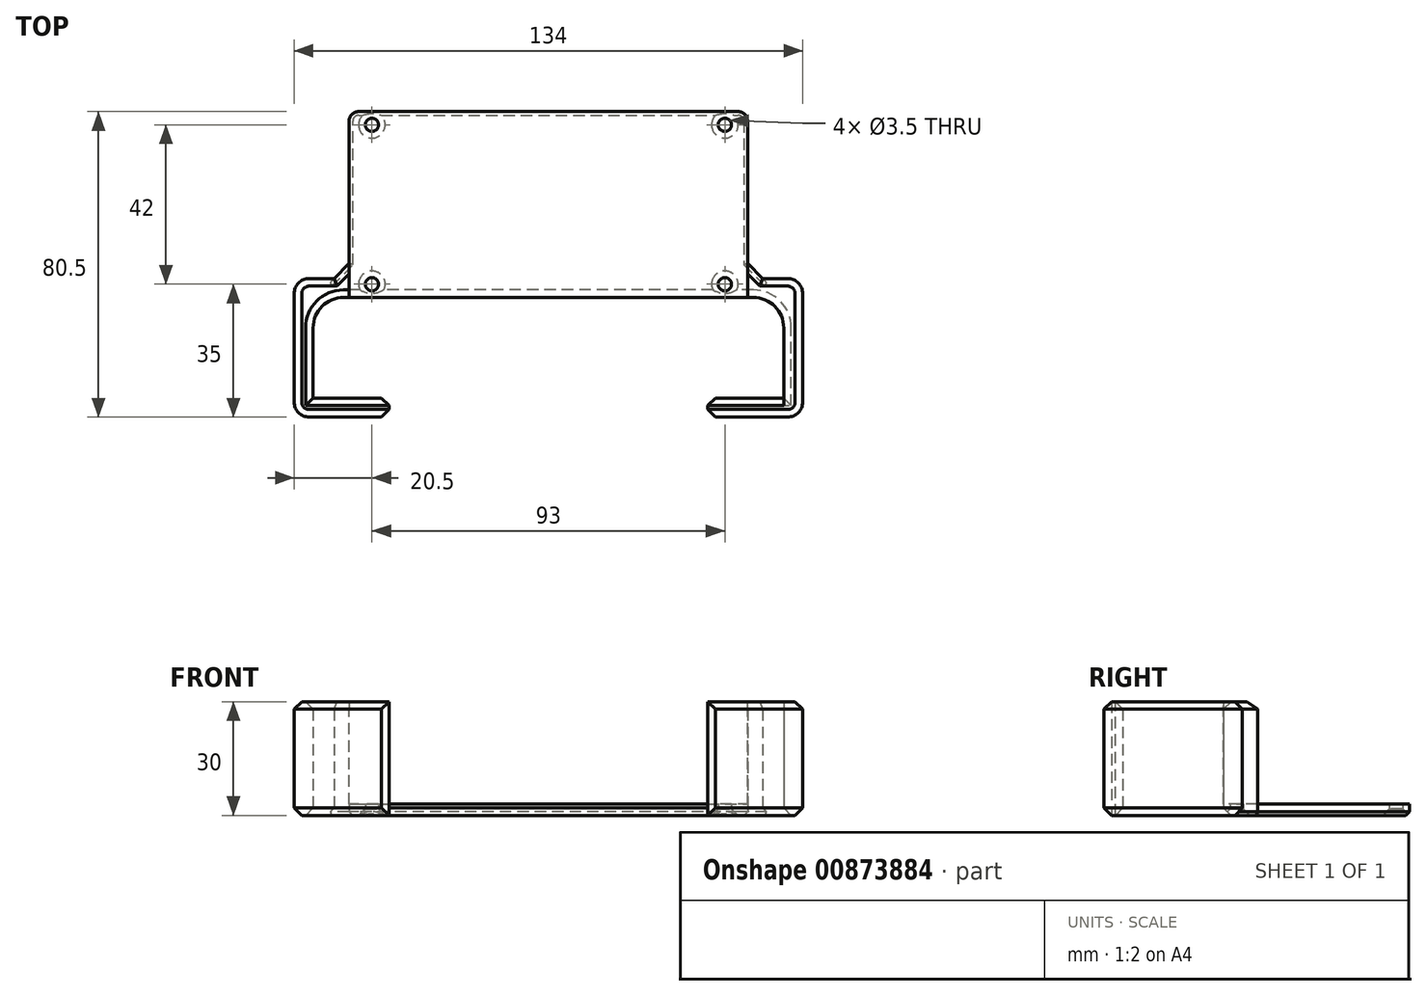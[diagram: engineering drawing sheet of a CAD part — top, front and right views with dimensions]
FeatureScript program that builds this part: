
annotation { "Feature Type Name" : "Feature", "Feature Type Description" : "" }
export const myFeature = defineFeature(function(context is Context, id is Id, definition is map)
    precondition{}
    {
        {
            var Q0;
            Q0=qCreatedBy(makeId("Top.planeOp"),FACE);
            var sketch = newSketch(context, id + "F0", { "sketchPlane" : qUnion([Q0])});
            skLineSegment(sketch, "E0.bottom", {"start": v(0, 0) * mm, "end": v(105, 0) * mm});
            skLineSegment(sketch, "E0.top", {"start": v(2.5, 49) * mm, "end": v(102.5, 49) * mm});
            skLineSegment(sketch, "E0.left", {"start": v(0, 9) * mm, "end": v(0, 46.5) * mm});
            skLineSegment(sketch, "E0.right", {"start": v(105, 9) * mm, "end": v(105, 46.5) * mm});
            skLineSegment(sketch, "E1.bottom", {"start": v(-1.5, 0) * mm, "end": v(106.5, 0) * mm});
            skLineSegment(sketch, "E1.top", {"start": v(-9.5, -26.5) * mm, "end": v(10.5, -26.5) * mm});
            skLineSegment(sketch, "E1.left", {"start": v(-9.5, -8) * mm, "end": v(-9.5, -26.5) * mm});
            skLineSegment(sketch, "E1.right", {"start": v(114.5, -8) * mm, "end": v(114.5, -26.5) * mm});
            skLineSegment(sketch, "E2.0", {"start": v(-10.5, 5) * mm, "end": v(-4, 5) * mm});
            skLineSegment(sketch, "E2.1", {"start": v(-14.5, 1) * mm, "end": v(-14.5, -27.5) * mm});
            skLineSegment(sketch, "E2.2", {"start": v(-10.5, -31.5) * mm, "end": v(10.5, -31.5) * mm});
            skLineSegment(sketch, "E2.3", {"start": v(119.5, 1) * mm, "end": v(119.5, -27.5) * mm});
            skLineSegment(sketch, "E3", {"start": v(10.5, -26.5) * mm, "end": v(10.5, -38.4) * mm});
            skLineSegment(sketch, "E4", {"start": v(94.5, -26.5) * mm, "end": v(94.5, -38.4) * mm});
            skLineSegment(sketch, "E5.trimOffspring", {"start": v(94.5, -26.5) * mm, "end": v(114.5, -26.5) * mm});
            skLineSegment(sketch, "E6.trimOffspring", {"start": v(94.5, -31.5) * mm, "end": v(115.5, -31.5) * mm});
            skLineSegment(sketch, "E7.trimOffspring", {"start": v(109, 5) * mm, "end": v(115.5, 5) * mm});
            skLineSegment(sketch, "E8", {"start": v(-4, 5) * mm, "end": v(0, 9) * mm});
            skPoint(sketch, "E9.orphan", {"position": v(0, 5) * mm});
            skLineSegment(sketch, "E10", {"start": v(105, 9) * mm, "end": v(109, 5) * mm});
            skPoint(sketch, "E11.visualSharp", {"position": v(-14.5, 5) * mm});
            skArc(sketch, "E11.filletArc", {"start": v(-10.5, 5) * mm, "mid": v(-13.33, 3.83) * mm, "end": v(-14.5, 1) * mm});
            skPoint(sketch, "E12.visualSharp", {"position": v(-14.5, -31.5) * mm});
            skArc(sketch, "E12.filletArc", {"start": v(-14.5, -27.5) * mm, "mid": v(-13.33, -30.33) * mm, "end": v(-10.5, -31.5) * mm});
            skPoint(sketch, "E13.visualSharp", {"position": v(119.5, -31.5) * mm});
            skArc(sketch, "E13.filletArc", {"start": v(115.5, -31.5) * mm, "mid": v(118.33, -30.33) * mm, "end": v(119.5, -27.5) * mm});
            skPoint(sketch, "E14.visualSharp", {"position": v(119.5, 5) * mm});
            skArc(sketch, "E14.filletArc", {"start": v(119.5, 1) * mm, "mid": v(118.33, 3.83) * mm, "end": v(115.5, 5) * mm});
            skPoint(sketch, "E15.visualSharp", {"position": v(0, 49) * mm});
            skArc(sketch, "E15.filletArc", {"start": v(2.5, 49) * mm, "mid": v(0.73, 48.27) * mm, "end": v(0, 46.5) * mm});
            skPoint(sketch, "E16.visualSharp", {"position": v(105, 49) * mm});
            skArc(sketch, "E16.filletArc", {"start": v(105, 46.5) * mm, "mid": v(104.27, 48.27) * mm, "end": v(102.5, 49) * mm});
            skPoint(sketch, "E17.visualSharp", {"position": v(-9.5, 0) * mm});
            skArc(sketch, "E17.filletArc", {"start": v(-1.5, 0) * mm, "mid": v(-7.16, -2.34) * mm, "end": v(-9.5, -8) * mm});
            skPoint(sketch, "E18.visualSharp", {"position": v(114.5, 0) * mm});
            skArc(sketch, "E18.filletArc", {"start": v(114.5, -8) * mm, "mid": v(112.16, -2.34) * mm, "end": v(106.5, 0) * mm});
            skSolve(sketch);
        }
        {
            var Q0;
            Q0=makeQuery(id+"F0.imprint","IMPRINT",FACE,{"disambiguationData":[TD([[makeQuery(id+"F0.imprint","IMPRINT",EDGE,{"derivedFrom":sQuery(id+"F0.wireOp",EDGE,"E0.top")}),-1.0]])]});
            extrude(context, id + "F1", {"entities" : qUnion([Q0]), "depth" : 30 * mm, "offsetDistance" : 25 * mm});
        }
        {
            var Q0;
            Q0=makeQuery(id+"F1.opExtrude","CAP_FACE",FACE,{"disambiguationData":[OSD([sQuery(id+"F0.wireOp",EDGE,"E0.top"),sQuery(id+"F0.wireOp",EDGE,"E0.left"),sQuery(id+"F0.wireOp",EDGE,"E0.right"),sQuery(id+"F0.wireOp",EDGE,"E1.bottom"),sQuery(id+"F0.wireOp",EDGE,"E1.top"),sQuery(id+"F0.wireOp",EDGE,"E1.left"),sQuery(id+"F0.wireOp",EDGE,"E1.right"),sQuery(id+"F0.wireOp",EDGE,"E2.0"),sQuery(id+"F0.wireOp",EDGE,"E2.1"),sQuery(id+"F0.wireOp",EDGE,"E2.2"),sQuery(id+"F0.wireOp",EDGE,"E2.3"),sQuery(id+"F0.wireOp",EDGE,"E3"),sQuery(id+"F0.wireOp",EDGE,"E4"),sQuery(id+"F0.wireOp",EDGE,"E5.trimOffspring"),sQuery(id+"F0.wireOp",EDGE,"E6.trimOffspring"),sQuery(id+"F0.wireOp",EDGE,"E7.trimOffspring"),sQuery(id+"F0.wireOp",EDGE,"E8"),sQuery(id+"F0.wireOp",EDGE,"E10"),sQuery(id+"F0.wireOp",EDGE,"E11.filletArc"),sQuery(id+"F0.wireOp",EDGE,"E12.filletArc"),sQuery(id+"F0.wireOp",EDGE,"E13.filletArc"),sQuery(id+"F0.wireOp",EDGE,"E14.filletArc"),sQuery(id+"F0.wireOp",EDGE,"E15.filletArc"),sQuery(id+"F0.wireOp",EDGE,"E16.filletArc"),sQuery(id+"F0.wireOp",EDGE,"E17.filletArc"),sQuery(id+"F0.wireOp",EDGE,"E18.filletArc")])],"isStart":false});
            var sketch = newSketch(context, id + "F2", { "sketchPlane" : qUnion([Q0])});
            skLineSegment(sketch, "E19.0.0", {"start": v(114.5, -26.5) * mm, "end": v(94.5, -26.5) * mm});
            skLineSegment(sketch, "E19.0.1", {"start": v(94.5, -26.5) * mm, "end": v(94.5, -31.5) * mm});
            skLineSegment(sketch, "E19.0.2", {"start": v(94.5, -31.5) * mm, "end": v(115.5, -31.5) * mm});
            skArc(sketch, "E19.0.3", {"start": v(115.5, -31.5) * mm, "mid": v(118.33, -30.33) * mm, "end": v(119.5, -27.5) * mm});
            skLineSegment(sketch, "E19.0.4", {"start": v(119.5, -27.5) * mm, "end": v(119.5, 1) * mm});
            skArc(sketch, "E19.0.5", {"start": v(119.5, 1) * mm, "mid": v(118.33, 3.83) * mm, "end": v(115.5, 5) * mm});
            skLineSegment(sketch, "E19.0.6", {"start": v(115.5, 5) * mm, "end": v(109, 5) * mm});
            skLineSegment(sketch, "E19.0.7", {"start": v(109, 5) * mm, "end": v(105, 9) * mm});
            skLineSegment(sketch, "E19.0.8", {"start": v(105, 9) * mm, "end": v(105, 46.5) * mm});
            skArc(sketch, "E19.0.9", {"start": v(105, 46.5) * mm, "mid": v(104.27, 48.27) * mm, "end": v(102.5, 49) * mm});
            skLineSegment(sketch, "E19.0.10", {"start": v(102.5, 49) * mm, "end": v(2.5, 49) * mm});
            skArc(sketch, "E19.0.11", {"start": v(2.5, 49) * mm, "mid": v(0.73, 48.27) * mm, "end": v(0, 46.5) * mm});
            skLineSegment(sketch, "E19.0.12", {"start": v(0, 46.5) * mm, "end": v(0, 9) * mm});
            skLineSegment(sketch, "E19.0.13", {"start": v(0, 9) * mm, "end": v(-4, 5) * mm});
            skLineSegment(sketch, "E19.0.14", {"start": v(-4, 5) * mm, "end": v(-10.5, 5) * mm});
            skArc(sketch, "E19.0.15", {"start": v(-10.5, 5) * mm, "mid": v(-13.33, 3.83) * mm, "end": v(-14.5, 1) * mm});
            skLineSegment(sketch, "E19.0.16", {"start": v(-14.5, 1) * mm, "end": v(-14.5, -27.5) * mm});
            skArc(sketch, "E19.0.17", {"start": v(-14.5, -27.5) * mm, "mid": v(-13.33, -30.33) * mm, "end": v(-10.5, -31.5) * mm});
            skLineSegment(sketch, "E19.0.18", {"start": v(-10.5, -31.5) * mm, "end": v(10.5, -31.5) * mm});
            skLineSegment(sketch, "E19.0.19", {"start": v(10.5, -31.5) * mm, "end": v(10.5, -26.5) * mm});
            skLineSegment(sketch, "E19.0.20", {"start": v(10.5, -26.5) * mm, "end": v(-9.5, -26.5) * mm});
            skLineSegment(sketch, "E19.0.21", {"start": v(-9.5, -26.5) * mm, "end": v(-9.5, -8) * mm});
            skArc(sketch, "E19.0.22", {"start": v(-9.5, -8) * mm, "mid": v(-7.16, -2.34) * mm, "end": v(-1.5, 0) * mm});
            skLineSegment(sketch, "E19.0.23", {"start": v(-1.5, 0) * mm, "end": v(106.5, 0) * mm});
            skArc(sketch, "E19.0.24", {"start": v(106.5, 0) * mm, "mid": v(112.16, -2.34) * mm, "end": v(114.5, -8) * mm});
            skLineSegment(sketch, "E19.0.25", {"start": v(114.5, -8) * mm, "end": v(114.5, -26.5) * mm});
            skLineSegment(sketch, "E20.bottom", {"start": v(0, 49.1) * mm, "end": v(105, 49.1) * mm});
            skLineSegment(sketch, "E20.left", {"start": v(0, 49.1) * mm, "end": v(0, 5) * mm});
            skLineSegment(sketch, "E20.right", {"start": v(105, 49.1) * mm, "end": v(105, 5) * mm});
            skLineSegment(sketch, "E21.top", {"start": v(0, 0) * mm, "end": v(105, 0) * mm});
            skLineSegment(sketch, "E21.left", {"start": v(0, 5) * mm, "end": v(0, 0) * mm});
            skLineSegment(sketch, "E21.right", {"start": v(105, 5) * mm, "end": v(105, 0) * mm});
            skSolve(sketch);
        }
        {
            var Q0;
            {var subQ4=sQuery(id+"F2.wireOp",EDGE,"E19.0.9");Q0=makeQuery(id+"F2.imprint","IMPRINT",FACE,{"disambiguationData":[TD([[makeQuery(id+"F2.imprint","IMPRINT",EDGE,{"derivedFrom":subQ4}),1.0]])]});}
            extrude(context, id + "F3", {"entities" : qUnion([Q0]), "operationType" : NewBodyOperationType.REMOVE, "oppositeDirection" : true, "depth" : 27 * mm, "offsetDistance" : 25 * mm});
        }
        {
            var Q0;
            Q0=makeQuery(id+"F1.opExtrude","SWEPT_EDGE",EDGE,{"disambiguationData":[OSD([sQuery(id+"F0.wireOp",EDGE,"E4"),sQuery(id+"F0.wireOp",EDGE,"E5.trimOffspring")])]});
            var Q1;
            Q1=makeQuery(id+"F1.opExtrude","SWEPT_EDGE",EDGE,{"disambiguationData":[OSD([sQuery(id+"F0.wireOp",EDGE,"E4"),sQuery(id+"F0.wireOp",EDGE,"E6.trimOffspring")])]});
            var Q2;
            Q2=makeQuery(id+"F1.opExtrude","SWEPT_EDGE",EDGE,{"disambiguationData":[OSD([sQuery(id+"F0.wireOp",EDGE,"E2.2"),sQuery(id+"F0.wireOp",EDGE,"E3")])]});
            var Q3;
            Q3=makeQuery(id+"F1.opExtrude","SWEPT_EDGE",EDGE,{"disambiguationData":[OSD([sQuery(id+"F0.wireOp",EDGE,"E1.top"),sQuery(id+"F0.wireOp",EDGE,"E3")])]});
            chamfer(context, id + "F4", {"entities" : qUnion([Q0, Q1, Q2, Q3]), "width" : 2 * mm, "tangentPropagation" : true});
        }
        {
            var Q0;
            Q0=makeQuery(id+"F1.opExtrude","CAP_EDGE",EDGE,{"disambiguationData":[OSD([sQuery(id+"F0.wireOp",EDGE,"E5.trimOffspring")])],"isStart":true});
            var Q1;
            Q1=makeQuery(id+"F1.opExtrude","CAP_EDGE",EDGE,{"disambiguationData":[OSD([sQuery(id+"F0.wireOp",EDGE,"E1.top")])],"isStart":true});
            var Q2;
            Q2=makeQuery(id+"F1.opExtrude","CAP_EDGE",EDGE,{"disambiguationData":[OSD([sQuery(id+"F0.wireOp",EDGE,"E2.2")])],"isStart":true});
            var Q3;
            Q3=makeQuery(id+"F1.opExtrude","CAP_EDGE",EDGE,{"disambiguationData":[OSD([sQuery(id+"F0.wireOp",EDGE,"E6.trimOffspring")])],"isStart":true});
            var Q4;
            Q4=makeQuery(id+"F1.opExtrude","CAP_EDGE",EDGE,{"disambiguationData":[OSD([sQuery(id+"F0.wireOp",EDGE,"E2.0")])],"isStart":false});
            var Q5;
            Q5=makeQuery(id+"F1.opExtrude","CAP_EDGE",EDGE,{"disambiguationData":[OSD([sQuery(id+"F0.wireOp",EDGE,"E1.left")])],"isStart":false});
            var Q6;
            Q6=makeQuery(id+"F1.opExtrude","CAP_EDGE",EDGE,{"disambiguationData":[OSD([sQuery(id+"F0.wireOp",EDGE,"E1.top")])],"isStart":false});
            var Q7;
            Q7=makeQuery(id+"F1.opExtrude","CAP_EDGE",EDGE,{"disambiguationData":[OSD([sQuery(id+"F0.wireOp",EDGE,"E5.trimOffspring")])],"isStart":false});
            var Q8;
            Q8=makeQuery(id+"F1.opExtrude","CAP_EDGE",EDGE,{"disambiguationData":[OSD([sQuery(id+"F0.wireOp",EDGE,"E6.trimOffspring")])],"isStart":false});
            var Q9;
            Q9=makeQuery(id+"F1.opExtrude","CAP_EDGE",EDGE,{"disambiguationData":[OSD([sQuery(id+"F0.wireOp",EDGE,"E10")])],"isStart":false});
            var Q10;
            Q10=makeQuery(id+"F1.opExtrude","CAP_EDGE",EDGE,{"disambiguationData":[OSD([sQuery(id+"F0.wireOp",EDGE,"E8")])],"isStart":false});
            chamfer(context, id + "F5", {"entities" : qUnion([Q0, Q1, Q2, Q3, Q4, Q5, Q6, Q7, Q8, Q9, Q10]), "width" : 2 * mm, "tangentPropagation" : true});
        }
        {
            var Q0;
            Q0=makeQuery(id+"F1.opExtrude","CAP_FACE",FACE,{"disambiguationData":[OSD([sQuery(id+"F0.wireOp",EDGE,"E0.top"),sQuery(id+"F0.wireOp",EDGE,"E0.left"),sQuery(id+"F0.wireOp",EDGE,"E0.right"),sQuery(id+"F0.wireOp",EDGE,"E1.bottom"),sQuery(id+"F0.wireOp",EDGE,"E1.top"),sQuery(id+"F0.wireOp",EDGE,"E1.left"),sQuery(id+"F0.wireOp",EDGE,"E1.right"),sQuery(id+"F0.wireOp",EDGE,"E2.0"),sQuery(id+"F0.wireOp",EDGE,"E2.1"),sQuery(id+"F0.wireOp",EDGE,"E2.2"),sQuery(id+"F0.wireOp",EDGE,"E2.3"),sQuery(id+"F0.wireOp",EDGE,"E3"),sQuery(id+"F0.wireOp",EDGE,"E4"),sQuery(id+"F0.wireOp",EDGE,"E5.trimOffspring"),sQuery(id+"F0.wireOp",EDGE,"E6.trimOffspring"),sQuery(id+"F0.wireOp",EDGE,"E7.trimOffspring"),sQuery(id+"F0.wireOp",EDGE,"E8"),sQuery(id+"F0.wireOp",EDGE,"E10"),sQuery(id+"F0.wireOp",EDGE,"E11.filletArc"),sQuery(id+"F0.wireOp",EDGE,"E12.filletArc"),sQuery(id+"F0.wireOp",EDGE,"E13.filletArc"),sQuery(id+"F0.wireOp",EDGE,"E14.filletArc"),sQuery(id+"F0.wireOp",EDGE,"E15.filletArc"),sQuery(id+"F0.wireOp",EDGE,"E16.filletArc"),sQuery(id+"F0.wireOp",EDGE,"E17.filletArc"),sQuery(id+"F0.wireOp",EDGE,"E18.filletArc")])],"isStart":true});
            var sketch = newSketch(context, id + "F6", { "sketchPlane" : qUnion([Q0])});
            skLineSegment(sketch, "E22.0.0", {"start": v(105, -9) * mm, "end": v(111, -3) * mm});
            skLineSegment(sketch, "E22.0.1", {"start": v(111, -3) * mm, "end": v(115.5, -3) * mm});
            skArc(sketch, "E22.0.2", {"start": v(115.5, -3) * mm, "mid": v(116.91, -2.41) * mm, "end": v(117.5, -1) * mm});
            skLineSegment(sketch, "E22.0.3", {"start": v(117.5, -1) * mm, "end": v(117.5, 27.5) * mm});
            skArc(sketch, "E22.0.4", {"start": v(117.5, 27.5) * mm, "mid": v(116.91, 28.91) * mm, "end": v(115.5, 29.5) * mm});
            skLineSegment(sketch, "E22.0.5", {"start": v(115.5, 29.5) * mm, "end": v(94.5, 29.5) * mm});
            skLineSegment(sketch, "E22.0.6", {"start": v(94.5, 29.5) * mm, "end": v(94.5, 28.5) * mm});
            skLineSegment(sketch, "E22.0.7", {"start": v(94.5, 28.5) * mm, "end": v(116.5, 28.5) * mm});
            skLineSegment(sketch, "E22.0.8", {"start": v(116.5, 28.5) * mm, "end": v(116.5, 8) * mm});
            skArc(sketch, "E22.0.9", {"start": v(116.5, 8) * mm, "mid": v(113.57, 0.93) * mm, "end": v(106.5, -2) * mm});
            skLineSegment(sketch, "E22.0.10", {"start": v(106.5, -2) * mm, "end": v(-1.5, -2) * mm});
            skArc(sketch, "E22.0.11", {"start": v(-1.5, -2) * mm, "mid": v(-8.57, 0.93) * mm, "end": v(-11.5, 8) * mm});
            skLineSegment(sketch, "E22.0.12", {"start": v(-11.5, 8) * mm, "end": v(-11.5, 28.5) * mm});
            skLineSegment(sketch, "E22.0.13", {"start": v(-11.5, 28.5) * mm, "end": v(10.5, 28.5) * mm});
            skLineSegment(sketch, "E22.0.14", {"start": v(10.5, 28.5) * mm, "end": v(10.5, 29.5) * mm});
            skLineSegment(sketch, "E22.0.15", {"start": v(10.5, 29.5) * mm, "end": v(-10.5, 29.5) * mm});
            skArc(sketch, "E22.0.16", {"start": v(-10.5, 29.5) * mm, "mid": v(-11.91, 28.91) * mm, "end": v(-12.5, 27.5) * mm});
            skLineSegment(sketch, "E22.0.17", {"start": v(-12.5, 27.5) * mm, "end": v(-12.5, -1) * mm});
            skArc(sketch, "E22.0.18", {"start": v(-12.5, -1) * mm, "mid": v(-11.91, -2.41) * mm, "end": v(-10.5, -3) * mm});
            skLineSegment(sketch, "E22.0.19", {"start": v(-10.5, -3) * mm, "end": v(-6, -3) * mm});
            skLineSegment(sketch, "E22.0.20", {"start": v(-6, -3) * mm, "end": v(0, -9) * mm});
            skLineSegment(sketch, "E22.0.21", {"start": v(0, -9) * mm, "end": v(0, -46.5) * mm});
            skArc(sketch, "E22.0.22", {"start": v(0, -46.5) * mm, "mid": v(0.73, -48.27) * mm, "end": v(2.5, -49) * mm});
            skLineSegment(sketch, "E22.0.23", {"start": v(2.5, -49) * mm, "end": v(102.5, -49) * mm});
            skArc(sketch, "E22.0.24", {"start": v(102.5, -49) * mm, "mid": v(104.27, -48.27) * mm, "end": v(105, -46.5) * mm});
            skLineSegment(sketch, "E22.0.25", {"start": v(105, -46.5) * mm, "end": v(105, -9) * mm});
            skPoint(sketch, "E23", {"position": v(6, -45.5) * mm});
            skPoint(sketch, "E24", {"position": v(6, -3.5) * mm});
            skPoint(sketch, "E25", {"position": v(99, -3.5) * mm});
            skPoint(sketch, "E26", {"position": v(99, -45.5) * mm});
            skSolve(sketch);
        }
        {
            var Q0;
            Q0=sQuery(id+"F6.wireOp",VERTEX,"E24");
            var Q1;
            Q1=sQuery(id+"F6.wireOp",VERTEX,"E23");
            var Q2;
            Q2=sQuery(id+"F6.wireOp",VERTEX,"E25");
            var Q3;
            Q3=sQuery(id+"F6.wireOp",VERTEX,"E26");
            var Q4;
            Q4=makeQuery(id+"F1.opExtrude","SWEPT_BODY",BODY,{"disambiguationData":[OSD([sQuery(id+"F0.wireOp",EDGE,"E0.top"),sQuery(id+"F0.wireOp",EDGE,"E0.left"),sQuery(id+"F0.wireOp",EDGE,"E0.right"),sQuery(id+"F0.wireOp",EDGE,"E1.bottom"),sQuery(id+"F0.wireOp",EDGE,"E1.top"),sQuery(id+"F0.wireOp",EDGE,"E1.left"),sQuery(id+"F0.wireOp",EDGE,"E1.right"),sQuery(id+"F0.wireOp",EDGE,"E2.0"),sQuery(id+"F0.wireOp",EDGE,"E2.1"),sQuery(id+"F0.wireOp",EDGE,"E2.2"),sQuery(id+"F0.wireOp",EDGE,"E2.3"),sQuery(id+"F0.wireOp",EDGE,"E3"),sQuery(id+"F0.wireOp",EDGE,"E4"),sQuery(id+"F0.wireOp",EDGE,"E5.trimOffspring"),sQuery(id+"F0.wireOp",EDGE,"E6.trimOffspring"),sQuery(id+"F0.wireOp",EDGE,"E7.trimOffspring"),sQuery(id+"F0.wireOp",EDGE,"E8"),sQuery(id+"F0.wireOp",EDGE,"E10"),sQuery(id+"F0.wireOp",EDGE,"E11.filletArc"),sQuery(id+"F0.wireOp",EDGE,"E12.filletArc"),sQuery(id+"F0.wireOp",EDGE,"E13.filletArc"),sQuery(id+"F0.wireOp",EDGE,"E14.filletArc"),sQuery(id+"F0.wireOp",EDGE,"E15.filletArc"),sQuery(id+"F0.wireOp",EDGE,"E16.filletArc"),sQuery(id+"F0.wireOp",EDGE,"E17.filletArc"),sQuery(id+"F0.wireOp",EDGE,"E18.filletArc")])]});
            hole(context, id + "F7", {"style" : HoleStyle.C_SINK, "endStyle" : HoleEndStyle.THROUGH, "holeDiameter" : 3.5 * mm, "cSinkDiameter" : 7 * mm, "cSinkAngle" : 90 * degree, "majorDiameter" : 5 * mm, "isTappedThrough" : true, "tappedDepth" : 12 * mm, "tapClearance" : 3, "locations" : qUnion([Q0, Q1, Q2, Q3]), "scope" : qUnion([Q4])});
        }
        {
            var Q0;
            {var subQ0=sQuery(id+"F0.wireOp",EDGE,"E18.filletArc");var subQ1=sQuery(id+"F0.wireOp",EDGE,"E1.bottom");var subQ4=makeQuery(id+"F7.hole-0.opRevolve","SWEPT_FACE",FACE,{"disambiguationData":[OSD([sQuery(id+"F7.hole-0.sketch.wireOp",EDGE,"csink_start_line_1")])]});Q0=makeQuery(id+"F7.hole-2.boolean.opBoolean","SPLIT",EDGE,{"disambiguationData":[TD([makeQuery(id+"F7.hole-0.boolean.opBoolean","COPY",FACE,{"derivedFrom":subQ4})])],"derivedFrom":makeQuery(id+"F7.hole-0.boolean.opBoolean","SPLIT",EDGE,{"disambiguationData":[TD([makeQuery(id+"F1.opExtrude","SWEPT_FACE",FACE,{"disambiguationData":[OSD([subQ0])]})])],"derivedFrom":makeQuery(id+"F1.opExtrude","CAP_EDGE",EDGE,{"disambiguationData":[OSD([subQ1])],"isStart":true})})});}
            chamfer(context, id + "F8", {"entities" : qUnion([Q0]), "width" : 2 * mm, "tangentPropagation" : true});
        }
        {
            var Q0;
            Q0=makeQuery(id+"F1.opExtrude","CAP_EDGE",EDGE,{"disambiguationData":[OSD([sQuery(id+"F0.wireOp",EDGE,"E0.left")])],"isStart":true});
            var Q1;
            Q1=makeQuery(id+"F1.opExtrude","CAP_EDGE",EDGE,{"disambiguationData":[OSD([sQuery(id+"F0.wireOp",EDGE,"E8")])],"isStart":true});
            var Q2;
            Q2=makeQuery(id+"F1.opExtrude","CAP_EDGE",EDGE,{"disambiguationData":[OSD([sQuery(id+"F0.wireOp",EDGE,"E10")])],"isStart":true});
            chamfer(context, id + "F9", {"entities" : qUnion([Q0, Q1, Q2]), "width" : 1 * mm, "tangentPropagation" : true});
        }
    });
